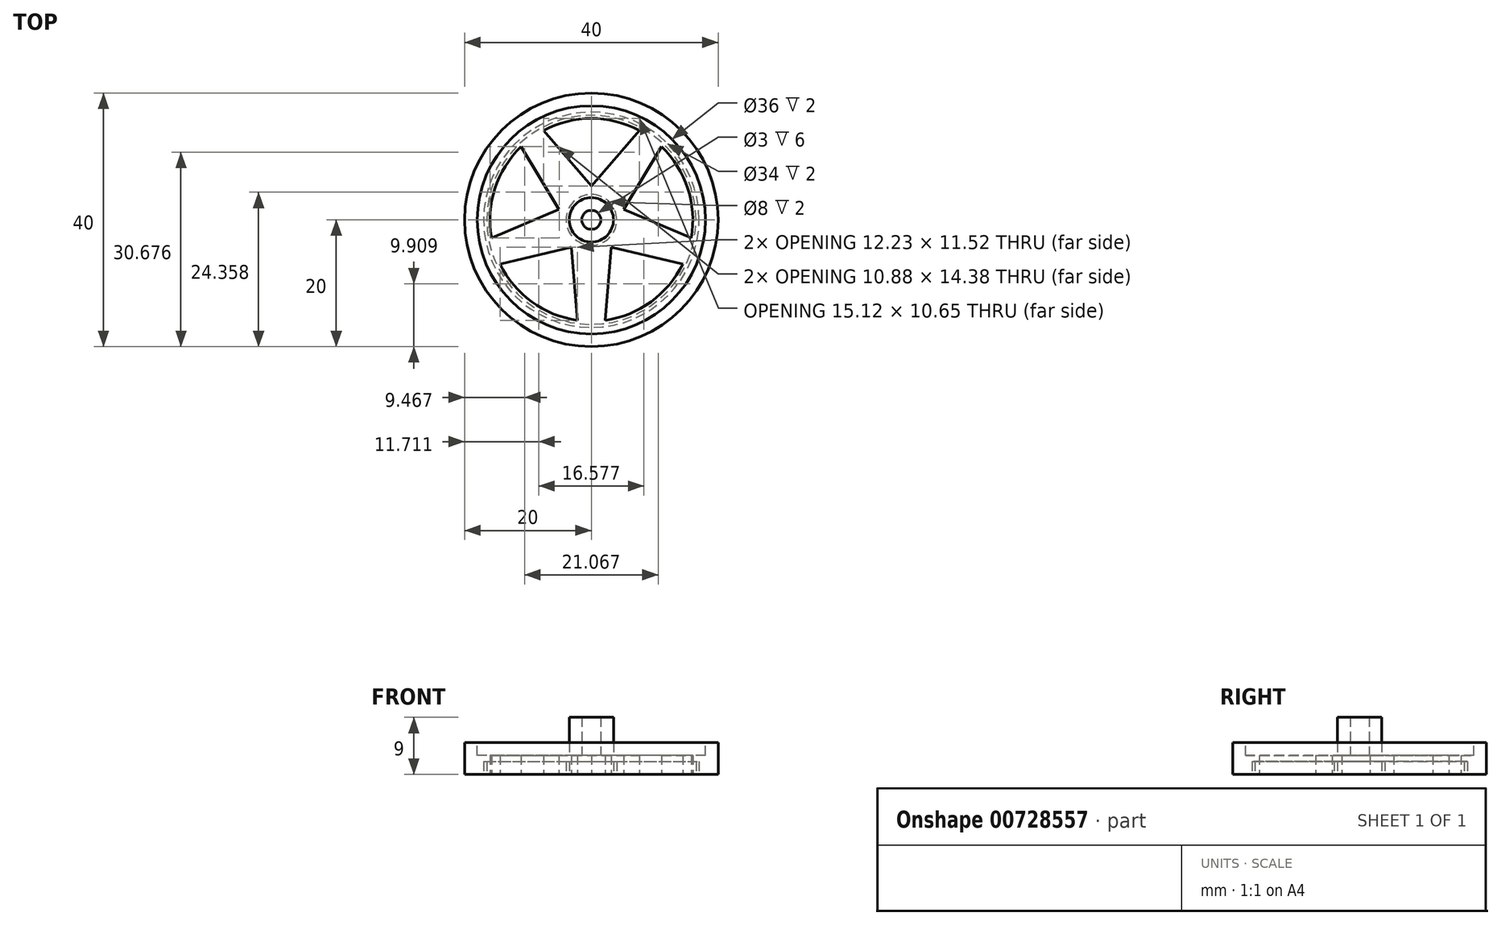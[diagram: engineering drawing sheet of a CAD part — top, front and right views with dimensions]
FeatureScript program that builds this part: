
annotation { "Feature Type Name" : "Feature", "Feature Type Description" : "" }
export const myFeature = defineFeature(function(context is Context, id is Id, definition is map)
    precondition{}
    {
        {
            var Q0;
            Q0=qCreatedBy(makeId("Top.planeOp"),FACE);
            var sketch = newSketch(context, id + "F0", { "sketchPlane" : qUnion([Q0])});
            skCircle(sketch, "E0", {"center": v(0, 0) * mm, "radius": 20 * mm});
            skSolve(sketch);
        }
        {
            var Q0;
            Q0=makeQuery(id+"F0.imprint","IMPRINT",FACE,{"disambiguationData":[TD([[makeQuery(id+"F0.imprint","IMPRINT",EDGE,{"derivedFrom":sQuery(id+"F0.wireOp",EDGE,"E0")}),1.0]])]});
            var Q1;
            Q1 = qSketchRegion(id + "F2", true);
            extrude(context, id + "F1", {"entities" : qUnion([Q0, Q1]), "depth" : 5 * mm, "offsetDistance" : 25 * mm});
        }
        {
            var Q0;
            Q0=makeQuery(id+"F1.opExtrude","CAP_FACE",FACE,{"disambiguationData":[OSD([sQuery(id+"F0.wireOp",EDGE,"E0")])],"isStart":false});
            var sketch = newSketch(context, id + "F2", { "sketchPlane" : qUnion([Q0])});
            skCircle(sketch, "E1", {"center": v(0, 0) * mm, "radius": 18 * mm});
            skSolve(sketch);
        }
        {
            var Q0;
            Q0=makeQuery(id+"F2.imprint","IMPRINT",FACE,{"disambiguationData":[TD([[makeQuery(id+"F2.imprint","IMPRINT",EDGE,{"derivedFrom":sQuery(id+"F2.wireOp",EDGE,"E1")}),1.0]])]});
            extrude(context, id + "F3", {"entities" : qUnion([Q0]), "operationType" : NewBodyOperationType.REMOVE, "oppositeDirection" : true, "depth" : 2 * mm, "offsetDistance" : 25 * mm});
        }
        {
            var Q0;
            Q0=makeQuery(id+"F3.boolean.opBoolean","COPY",FACE,{"derivedFrom":makeQuery(id+"F3.opExtrude","CAP_FACE",FACE,{"disambiguationData":[OSD([sQuery(id+"F2.wireOp",EDGE,"E1")])],"isStart":false})});
            var sketch = newSketch(context, id + "F4", { "sketchPlane" : qUnion([Q0])});
            skCircle(sketch, "E2", {"center": v(0, 0) * mm, "radius": 1.5 * mm});
            skCircle(sketch, "E3", {"center": v(0, 0) * mm, "radius": 3.5 * mm});
            skSolve(sketch);
        }
        {
            var Q0;
            Q0=makeQuery(id+"F1.opExtrude","CAP_FACE",FACE,{"disambiguationData":[OSD([sQuery(id+"F0.wireOp",EDGE,"E0")])],"isStart":true});
            var sketch = newSketch(context, id + "F5", { "sketchPlane" : qUnion([Q0])});
            skLineSegment(sketch, "E4", {"start": v(0, 0) * mm, "end": v(2, 0) * mm});
            skLineSegment(sketch, "E5", {"start": v(2.17, 15.85) * mm, "end": v(3.15, 4.33) * mm});
            skLineSegment(sketch, "E6.MirrorCS", {"start": v(-2.17, 15.85) * mm, "end": v(-3.15, 4.33) * mm});
            skLineSegment(sketch, "E7.1.0", {"start": v(-15.75, 2.83) * mm, "end": v(-5.1, -1.65) * mm});
            skLineSegment(sketch, "E7.1.4", {"start": v(-14.4, 6.96) * mm, "end": v(-3.15, 4.33) * mm});
            skLineSegment(sketch, "E7.2.0", {"start": v(-7.56, -14.1) * mm, "end": v(0, -5.35) * mm});
            skLineSegment(sketch, "E7.2.4", {"start": v(-11.07, -11.55) * mm, "end": v(-5.1, -1.65) * mm});
            skLineSegment(sketch, "E7.3.0", {"start": v(11.07, -11.55) * mm, "end": v(5.1, -1.65) * mm});
            skLineSegment(sketch, "E7.3.4", {"start": v(7.56, -14.1) * mm, "end": v(0, -5.35) * mm});
            skLineSegment(sketch, "E7.4.0", {"start": v(14.4, 6.96) * mm, "end": v(3.15, 4.33) * mm});
            skLineSegment(sketch, "E7.4.4", {"start": v(15.75, 2.83) * mm, "end": v(5.1, -1.65) * mm});
            skPoint(sketch, "E7.center", {"position": v(0, 0) * mm});
            skArc(sketch, "E8", {"start": v(-2.17, 15.85) * mm, "mid": v(-9.4, 12.94) * mm, "end": v(-14.4, 6.96) * mm});
            skPoint(sketch, "E9.orphan", {"position": v(-2, 17.89) * mm});
            skPoint(sketch, "E10.trimOffspring.end.orphan", {"position": v(2, 17.89) * mm});
            skPoint(sketch, "E11.orphan", {"position": v(16.4, 7.43) * mm});
            skPoint(sketch, "E12.orphan", {"position": v(17.63, 3.63) * mm});
            skPoint(sketch, "E13.orphan", {"position": v(12.13, -13.3) * mm});
            skPoint(sketch, "E14.orphan", {"position": v(-8.9, -15.65) * mm});
            skPoint(sketch, "E15.orphan", {"position": v(-17.63, 3.63) * mm});
            skPoint(sketch, "E16.orphan", {"position": v(-16.4, 7.43) * mm});
            skCircle(sketch, "E17", {"center": v(0, 0) * mm, "radius": 16.5 * mm});
            skCircle(sketch, "E18", {"center": v(0, 0) * mm, "radius": 17 * mm});
            skArc(sketch, "E19.trimOffspring", {"start": v(14.4, 6.96) * mm, "mid": v(9.4, 12.94) * mm, "end": v(2.17, 15.85) * mm});
            skArc(sketch, "E20.trimOffspring", {"start": v(11.07, -11.55) * mm, "mid": v(15.22, -4.94) * mm, "end": v(15.75, 2.83) * mm});
            skArc(sketch, "E21.trimOffspring", {"start": v(-7.56, -14.1) * mm, "mid": v(0, -16) * mm, "end": v(7.56, -14.1) * mm});
            skArc(sketch, "E22.trimOffspring", {"start": v(-15.75, 2.83) * mm, "mid": v(-15.22, -4.94) * mm, "end": v(-11.07, -11.55) * mm});
            skSolve(sketch);
        }
        {
            var Q0;
            Q0=makeQuery(id+"F4.imprint","IMPRINT",FACE,{"disambiguationData":[TD([[makeQuery(id+"F4.imprint","IMPRINT",EDGE,{"derivedFrom":sQuery(id+"F4.wireOp",EDGE,"E2")}),-1.0]])]});
            extrude(context, id + "F6", {"entities" : qUnion([Q0]), "operationType" : NewBodyOperationType.ADD, "depth" : 6 * mm, "offsetDistance" : 25 * mm});
        }
        {
            var Q0;
            Q0=makeQuery(id+"F5.imprint","IMPRINT",FACE,{"disambiguationData":[TD([[makeQuery(id+"F5.imprint","IMPRINT",EDGE,{"derivedFrom":sQuery(id+"F5.wireOp",EDGE,"E7.2.0")}),-1.0]])]});
            var Q1;
            Q1=makeQuery(id+"F5.imprint","IMPRINT",FACE,{"disambiguationData":[TD([[makeQuery(id+"F5.imprint","IMPRINT",EDGE,{"derivedFrom":sQuery(id+"F5.wireOp",EDGE,"E7.1.0")}),-1.0]])]});
            var Q2;
            Q2=makeQuery(id+"F5.imprint","IMPRINT",FACE,{"disambiguationData":[TD([[makeQuery(id+"F5.imprint","IMPRINT",EDGE,{"derivedFrom":sQuery(id+"F5.wireOp",EDGE,"E6.MirrorCS")}),-1.0]])]});
            var Q3;
            Q3=makeQuery(id+"F5.imprint","IMPRINT",FACE,{"disambiguationData":[TD([[makeQuery(id+"F5.imprint","IMPRINT",EDGE,{"derivedFrom":sQuery(id+"F5.wireOp",EDGE,"E5")}),1.0]])]});
            var Q4;
            Q4=makeQuery(id+"F5.imprint","IMPRINT",FACE,{"disambiguationData":[TD([[makeQuery(id+"F5.imprint","IMPRINT",EDGE,{"derivedFrom":sQuery(id+"F5.wireOp",EDGE,"E7.3.0")}),-1.0]])]});
            var Q5;
            Q5=makeQuery(id+"F6.opExtrude","CAP_FACE",FACE,{"disambiguationData":[OSD([sQuery(id+"F4.wireOp",EDGE,"E2"),sQuery(id+"F4.wireOp",EDGE,"E3")])],"isStart":false});
            extrude(context, id + "F7", {"entities" : qUnion([Q0, Q1, Q2, Q3, Q4, Q5]), "operationType" : NewBodyOperationType.REMOVE, "oppositeDirection" : true, "depth" : 3 * mm, "offsetDistance" : 25 * mm});
        }
        {
            var Q0;
            Q0=qSketchRegion(id+"F5",true);
            extrude(context, id + "F8", {"entities" : qUnion([Q0]), "operationType" : NewBodyOperationType.REMOVE, "oppositeDirection" : true, "depth" : 2 * mm, "offsetDistance" : 25 * mm});
        }
        {
            var Q0;
            Q0=makeQuery(id+"F8.boolean.opBoolean","SPLIT",FACE,{"disambiguationData":[TD([makeQuery(id+"F7.boolean.opBoolean","COPY",FACE,{"derivedFrom":makeQuery(id+"F7.opExtrude","SWEPT_FACE",FACE,{"disambiguationData":[OSD([sQuery(id+"F5.wireOp",EDGE,"E5")])]})})])],"derivedFrom":makeQuery(id+"F1.opExtrude","CAP_FACE",FACE,{"disambiguationData":[OSD([sQuery(id+"F0.wireOp",EDGE,"E0")])],"isStart":true})});
            var sketch = newSketch(context, id + "F9", { "sketchPlane" : qUnion([Q0])});
            skCircle(sketch, "E23", {"center": v(0, 0) * mm, "radius": 3.5 * mm});
            skCircle(sketch, "E24", {"center": v(0, 0) * mm, "radius": 4 * mm});
            skSolve(sketch);
        }
        {
            var Q0;
            Q0=makeQuery(id+"F9.imprint","IMPRINT",FACE,{"disambiguationData":[TD([[makeQuery(id+"F9.imprint","IMPRINT",EDGE,{"derivedFrom":sQuery(id+"F9.wireOp",EDGE,"E23")}),-1.0]])]});
            extrude(context, id + "F10", {"entities" : qUnion([Q0]), "operationType" : NewBodyOperationType.REMOVE, "oppositeDirection" : true, "depth" : 2 * mm, "offsetDistance" : 25 * mm});
        }
    });
